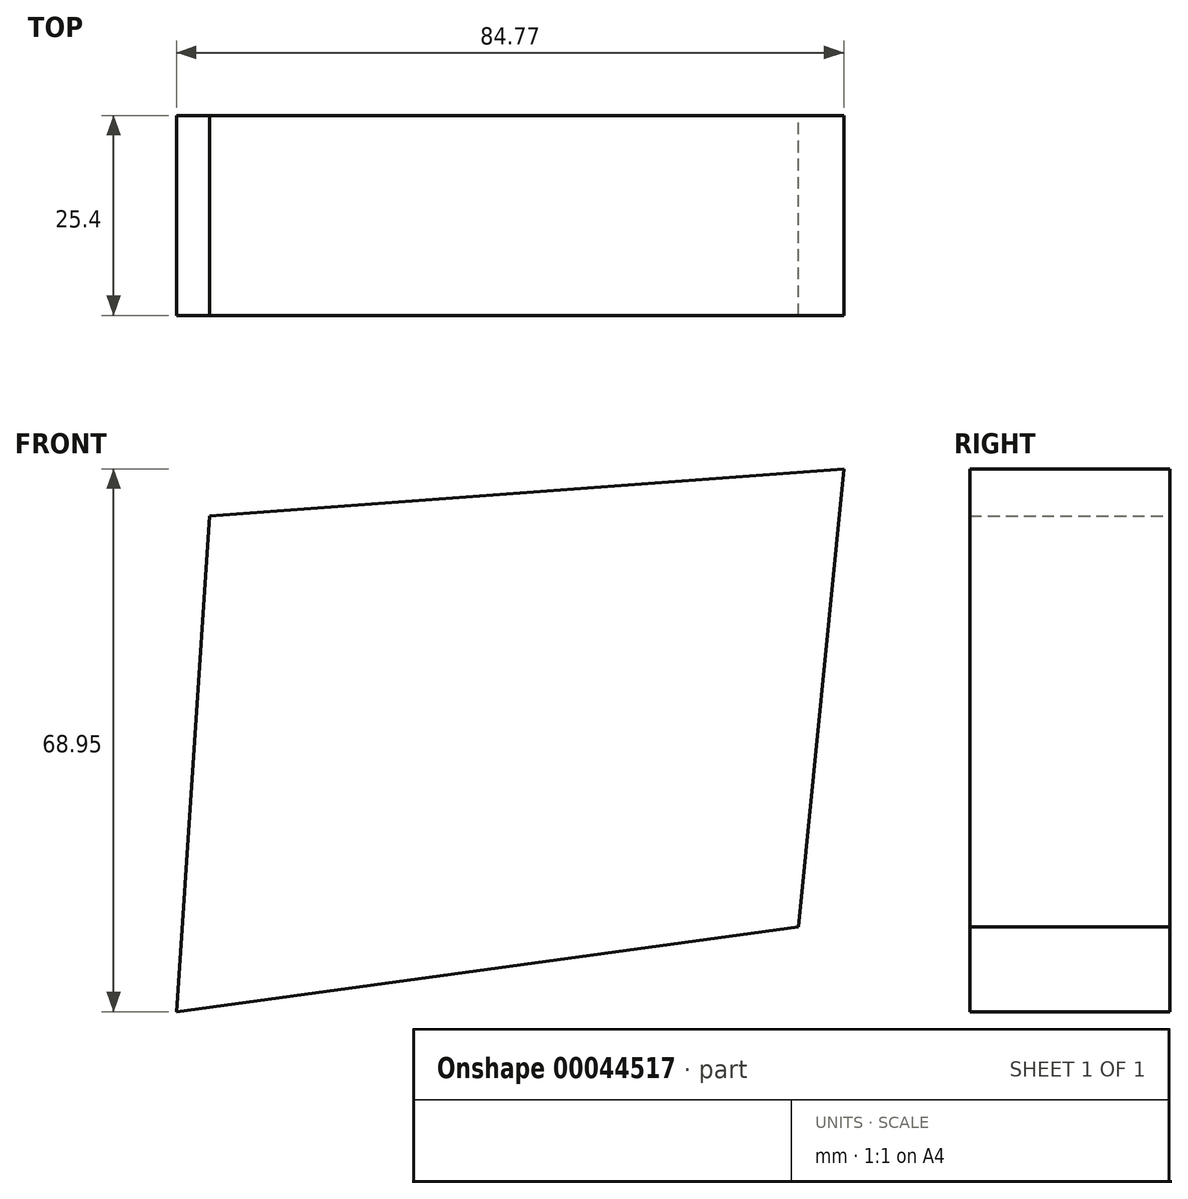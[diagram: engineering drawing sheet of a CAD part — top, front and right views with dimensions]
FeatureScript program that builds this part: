
annotation { "Feature Type Name" : "Feature", "Feature Type Description" : "" }
export const myFeature = defineFeature(function(context is Context, id is Id, definition is map)
    precondition{}
    {
        {
            var Q0;
            Q0=qCreatedBy(makeId("Front.planeOp"),FACE);
            var sketch = newSketch(context, id + "F0", { "sketchPlane" : qUnion([Q0])});
            skLineSegment(sketch, "E0", {"start": v(-52.33, 58.94) * mm, "end": v(28.26, 64.93) * mm});
            skLineSegment(sketch, "E1", {"start": v(28.26, 64.93) * mm, "end": v(22.5, 6.76) * mm});
            skLineSegment(sketch, "E2", {"start": v(22.5, 6.76) * mm, "end": v(-56.51, -4.02) * mm});
            skLineSegment(sketch, "E3", {"start": v(-56.51, -4.02) * mm, "end": v(-52.33, 58.94) * mm});
            skSolve(sketch);
        }
        {
            var Q0;
            Q0 = qSketchRegion(id + "F0", true);
            extrude(context, id + "F1", {"entities" : qUnion([Q0]), "depth" : 25.4 * mm});
        }
    });
